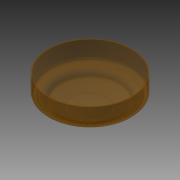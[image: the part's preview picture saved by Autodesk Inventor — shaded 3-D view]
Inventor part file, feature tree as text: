
AUTODESK INVENTOR PART (.ipt)
format: ipt  version: 2014 (Build 180170000, 170)  size: 190,976 bytes
history: native  units: in
note: dims shown in document units (in); Inventor stores cm internally (conversion verified against a paired STEP export)
features: reference x3, revolve x1, sketch x1
ambient origin geometry x8: Origin, YZ Plane, XZ Plane, XY Plane, X Axis, Y Axis, Z Axis, Center Point
bodies: Solid1 (feature_tree)
feature tree (5):
  revolve  "Revolution1"  [1 undecoded]
  sketch  "Sketch2"  dims[d8=0.0787in d9=0.01in d10=0.007in d11=90.0deg]
  reference  "Reference4"
  reference  "Reference5"
  reference  "Reference6"
note: 1 required parameter value undecoded (feature->parameter linkage not recoverable at this tier; creation-order binding heuristic only, values carry confidence <= 0.55)
